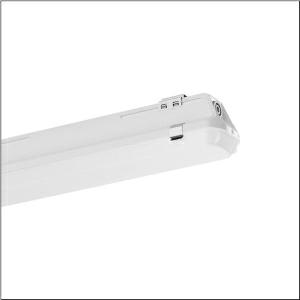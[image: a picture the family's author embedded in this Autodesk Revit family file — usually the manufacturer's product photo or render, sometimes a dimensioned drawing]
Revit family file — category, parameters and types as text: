
# Revit family: monsun_r__21_51fb107p480b005_c053
name_source: partatom
category: Lighting Fixtures
units: mm (PartAtom-declared; Revit-internal decimal feet)

## family parameters
Cut with Voids When Loaded = No
Host = Face
Light Source = No
Part Type = Normal
Room Calculation Point = No
Round Connector Dimension = Use Diameter
Shared = No

## types (1)
- Monsun® 21 (1 x LED, 8070 lm, 52.8 W, 4000K)
    Apparent Load = 53 VA
    CIE Flux Codes = 47 77 93 94 100
    Color Rendering = 80
    Color Temperature = 4000K
    Default Elevation = 1800 mm
    Description = Monsun® 21, damp-proof luminaire, chain hanger, primary optical cover: enclosure, of PMMA, light emission: direct distribution, primary light characteristic: symmetric, installation type: suspended mounting, surface-mounted, horizontal mounting, vertical mounting, LED, rated luminous flux: 8.070lm, luminous efficacy: 153lm/W, light colour: 840, colour temperature: 4000K, control gear: ECG, with terminal, 3-pole, max. 2.5mm², through-wiring: 5x 2.5mm², mains connection: 220..240V, AC, 50/60Hz, rated input power: 53W, housing, of glass-fibre reinforced polyester, uncoated, bright grey, incl. chain hanger, length: 1.590mm, width: 90mm, height: 88mm, clip for enclosure, of stainless steel (V2A), ceiling mounting element, of stainless steel (V2A), chain hanger, of stainless steel (V2A), protection rating (complete): IP66, insulation class (complete): insulation class I (protective earthing), certification: CE, ENEC, VDE, UKCA, protection symbol: D, impact resistance: IK04, permissible operating ambient temperature: -25..+35°C, standard: EN 50419, EN 60598-2-1, corresponds to IFS (International Featured Standards) requirements for safety and quality in the food industry, for indoor or canopied outdoor use, no direct snow, no direct sun, no direct rain, contact your sales advisor before using the luminaires in applications with unclear chemical exposure, large temperature fluctuations or condensation-forming humidity, LABS conformity tested according to VDMA 24364:2018-05, packaging unit: 1 piece
    Height = 89 mm
    Lamp = 1 x LED
    Lamp Light Flux = 8070 lm
    Lamp Power = 52.8 W
    Lamp count = 1
    Length = 1590 mm
    Luminous efficacy = 153 lm/W
    Manufacturer = Siteco
    ModVariant = No
    Model = 51FB107P480B005
    Mounting Place = Ceiling
    Mounting Type = Surface mounted
    Number of Poles = 1
    OnlyDefault = Yes
    Power Factor = 1
    Product Name = Monsun® 21
    Product group = damp-proof luminaire
    ProductGroupID = 300
    Protection Class = Protection class I
    Protection Degree = IP 66
    RLX_Detail_Level = 1
    RLX_Emergency_Light_Flux = 0 lm
    RLX_Emergency_Type = 0
    RLX_Emergency_Type_DB = No
    RlxData = <blob elided: 88633 chars, md5=eeb4db3f>
    Socket = socket
    Standby Power = 0 W
    System Light Flux = 8070 lm
    System Power = 53 W
    Type Comments = Product without accessories
    Type Image = l_1319656.jpg
    URL = http://relux.com
    VarID = ---
    Voltage = 0 V
    Weight = 0.00 kg
    Width = 90 mm

## geometry (parser evidence)
native form markers: Blend x4, Sweep x13
no freeform markers — native parametric forms only
